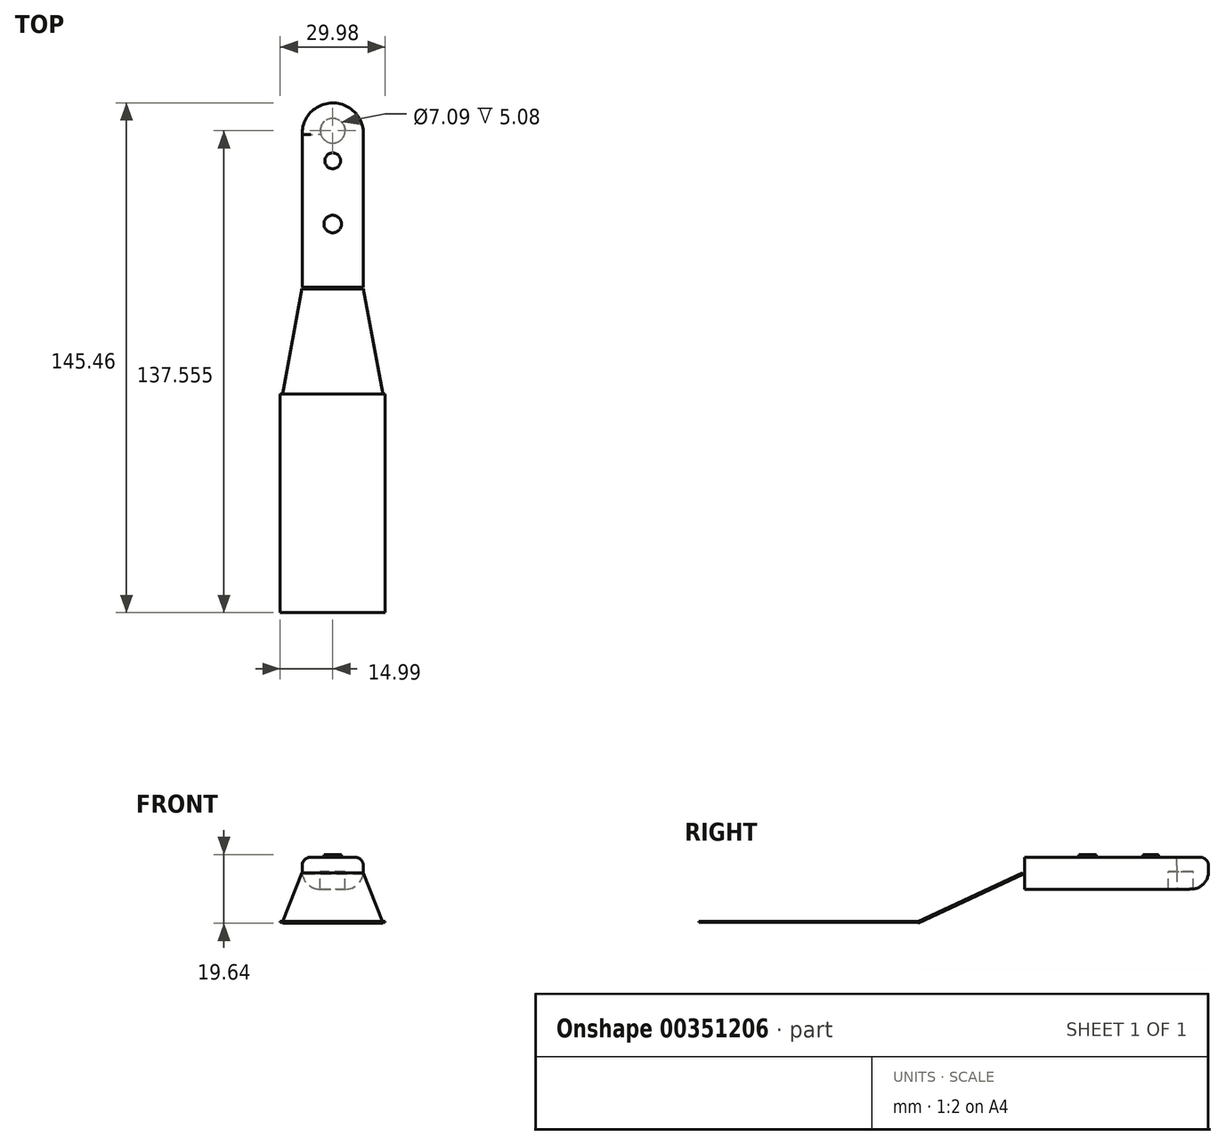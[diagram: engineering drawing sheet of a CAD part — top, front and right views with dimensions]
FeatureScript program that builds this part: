
annotation { "Feature Type Name" : "Feature", "Feature Type Description" : "" }
export const myFeature = defineFeature(function(context is Context, id is Id, definition is map)
    precondition{}
    {
        {
            var Q0;
            Q0=qCreatedBy(makeId("Right.planeOp"),FACE);
            var sketch = newSketch(context, id + "F0", { "sketchPlane" : qUnion([Q0])});
            skLineSegment(sketch, "E0.bottom", {"start": v(-69.47, -19.83) * mm, "end": v(-7.07, -19.83) * mm});
            skLineSegment(sketch, "E0.top", {"start": v(-69.47, -19.55) * mm, "end": v(-7.07, -19.55) * mm});
            skLineSegment(sketch, "E0.left", {"start": v(-69.47, -19.83) * mm, "end": v(-69.47, -19.55) * mm});
            skLineSegment(sketch, "E0.right", {"start": v(-7.07, -19.83) * mm, "end": v(-7.07, -19.55) * mm});
            skSolve(sketch);
        }
        {
            var Q0;
            Q0=qCreatedBy(makeId("Right.planeOp"),FACE);
            var sketch = newSketch(context, id + "F1", { "sketchPlane" : qUnion([Q0])});
            skSolve(sketch);
        }
        {
            var Q0;
            Q0 = qSketchRegion(id + "F1", true);
            var Q1;
            Q1 = qSketchRegion(id + "F0", true);
            extrude(context, id + "F2", {"entities" : qUnion([Q0, Q1]), "endBound" : BoundingType.SYMMETRIC, "depth" : 29.97 * mm});
        }
        {
            var Q0;
            Q0=qCreatedBy(makeId("Top.planeOp"),FACE);
            cPlane(context, id + "F3", {"entities" : qUnion([Q0]), "cplaneType" : CPlaneType.OFFSET, "offset" : 19.56 * mm, "oppositeDirection" : true, "width" : 152.4 * mm, "height" : 152.4 * mm});
        }
        {
            var Q0;
            Q0=qCreatedBy(id+"F3.planeOp",FACE);
            var sketch = newSketch(context, id + "F4", { "sketchPlane" : qUnion([Q0])});
            skLineSegment(sketch, "E1", {"start": v(0, -6.8) * mm, "end": v(75.85, -6.8) * mm, "construction": true});
            skSolve(sketch);
        }
        {
            var Q0;
            Q0=sQuery(id+"F4.wireOp",EDGE,"E1");
            cPlane(context, id + "F5", {"entities" : qUnion([Q0]), "cplaneType" : CPlaneType.LINE_ANGLE, "offset" : 25.4 * mm, "angle" : 65 * degree, "oppositeDirection" : true, "width" : 152.4 * mm, "height" : 152.4 * mm});
        }
        {
            var Q0;
            Q0=qCreatedBy(id+"F5.planeOp",FACE);
            var sketch = newSketch(context, id + "F6", { "sketchPlane" : qUnion([Q0])});
            skLineSegment(sketch, "E2", {"start": v(0, 14.73) * mm, "end": v(14.3, 14.73) * mm});
            skLineSegment(sketch, "E3", {"start": v(14.3, 14.73) * mm, "end": v(8.75, -18.32) * mm});
            skLineSegment(sketch, "E4", {"start": v(8.75, -18.32) * mm, "end": v(0, -18.32) * mm});
            skLineSegment(sketch, "E5", {"start": v(0, -18.32) * mm, "end": v(0, 14.73) * mm});
            skLineSegment(sketch, "E6.MirrorCS", {"start": v(-14.3, 14.73) * mm, "end": v(-8.75, -18.32) * mm});
            skLineSegment(sketch, "E7.MirrorCS", {"start": v(-8.75, -18.32) * mm, "end": v(0, -18.32) * mm});
            skLineSegment(sketch, "E8.MirrorCS", {"start": v(0, 14.73) * mm, "end": v(-14.3, 14.73) * mm});
            skSolve(sketch);
        }
        {
            var Q0;
            Q0 = qSketchRegion(id + "F6", true);
            extrude(context, id + "F7", {"entities" : qUnion([Q0]), "depth" : 0.5 * mm});
        }
        {
            var Q0;
            Q0=qCreatedBy(id+"F3.planeOp",FACE);
            cPlane(context, id + "F8", {"entities" : qUnion([Q0]), "cplaneType" : CPlaneType.OFFSET, "offset" : 13.72 * mm, "width" : 152.4 * mm, "height" : 152.4 * mm});
        }
        {
            var Q0;
            Q0=qCreatedBy(id+"F8.planeOp",FACE);
            var sketch = newSketch(context, id + "F9", { "sketchPlane" : qUnion([Q0])});
            skLineSegment(sketch, "E9", {"start": v(0, 23.43) * mm, "end": v(-8.72, 23.43) * mm});
            skLineSegment(sketch, "E10", {"start": v(-8.72, 23.43) * mm, "end": v(-8.72, 66.98) * mm});
            skLineSegment(sketch, "E11", {"start": v(0, 23.43) * mm, "end": v(8.75, 23.43) * mm});
            skLineSegment(sketch, "E12", {"start": v(8.75, 23.43) * mm, "end": v(8.75, 67.25) * mm});
            skArc(sketch, "E13", {"start": v(8.75, 67.25) * mm, "mid": v(-0.13, 75.99) * mm, "end": v(-8.72, 66.98) * mm});
            skSolve(sketch);
        }
        {
            var Q0;
            Q0=qCreatedBy(id+"F8.planeOp",FACE);
            var sketch = newSketch(context, id + "F10", { "sketchPlane" : qUnion([Q0])});
            skCircle(sketch, "E14", {"center": v(0, 59.49) * mm, "radius": 2.26 * mm});
            skCircle(sketch, "E15", {"center": v(0, 41.46) * mm, "radius": 2.5 * mm});
            skSolve(sketch);
        }
        {
            var Q0;
            Q0=makeQuery(id+"F9.imprint","IMPRINT",FACE,{"disambiguationData":[TD([[makeQuery(id+"F9.imprint","IMPRINT",EDGE,{"derivedFrom":sQuery(id+"F9.wireOp",EDGE,"E9")}),-1.0]])]});
            extrude(context, id + "F11", {"entities" : qUnion([Q0]), "endBound" : BoundingType.SYMMETRIC, "depth" : 9.14 * mm});
        }
        {
            var Q0;
            Q0 = qSketchRegion(id + "F10", true);
            extrude(context, id + "F12", {"entities" : qUnion([Q0]), "operationType" : NewBodyOperationType.ADD, "depth" : 5.33 * mm});
        }
        {
            var Q0;
            Q0=makeQuery(id+"F11.opExtrude","CAP_EDGE",EDGE,{"disambiguationData":[OSD([sQuery(id+"F9.wireOp",EDGE,"E10")])],"isStart":false});
            var Q1;
            Q1=makeQuery(id+"F11.opExtrude","CAP_EDGE",EDGE,{"disambiguationData":[OSD([sQuery(id+"F9.wireOp",EDGE,"E12")])],"isStart":false});
            fillet(context, id + "F13", {"entities" : qUnion([Q0, Q1]), "radius" : 2.45 * mm, "tangentPropagation" : true, "allowEdgeOverflow" : false});
        }
        {
            var Q0;
            Q0=makeQuery(id+"F11.opExtrude","CAP_EDGE",EDGE,{"disambiguationData":[OSD([sQuery(id+"F9.wireOp",EDGE,"E12")])],"isStart":true});
            fillet(context, id + "F14", {"entities" : qUnion([Q0]), "radius" : 5.08 * mm, "tangentPropagation" : true, "allowEdgeOverflow" : false});
        }
        {
            var Q0;
            Q0=qCreatedBy(makeId("Top.planeOp"),FACE);
            cPlane(context, id + "F15", {"entities" : qUnion([Q0]), "cplaneType" : CPlaneType.OFFSET, "offset" : 5.33 * mm, "oppositeDirection" : true, "width" : 152.4 * mm, "height" : 152.4 * mm});
        }
        {
            var Q0;
            Q0=qCreatedBy(id+"F15.planeOp",FACE);
            var sketch = newSketch(context, id + "F16", { "sketchPlane" : qUnion([Q0])});
            skCircle(sketch, "E16", {"center": v(0, 68.08) * mm, "radius": 3.54 * mm});
            skSolve(sketch);
        }
        {
            var Q0;
            Q0 = qSketchRegion(id + "F16", true);
            extrude(context, id + "F17", {"entities" : qUnion([Q0]), "operationType" : NewBodyOperationType.REMOVE, "oppositeDirection" : true, "depth" : 25.4 * mm});
        }
    });
